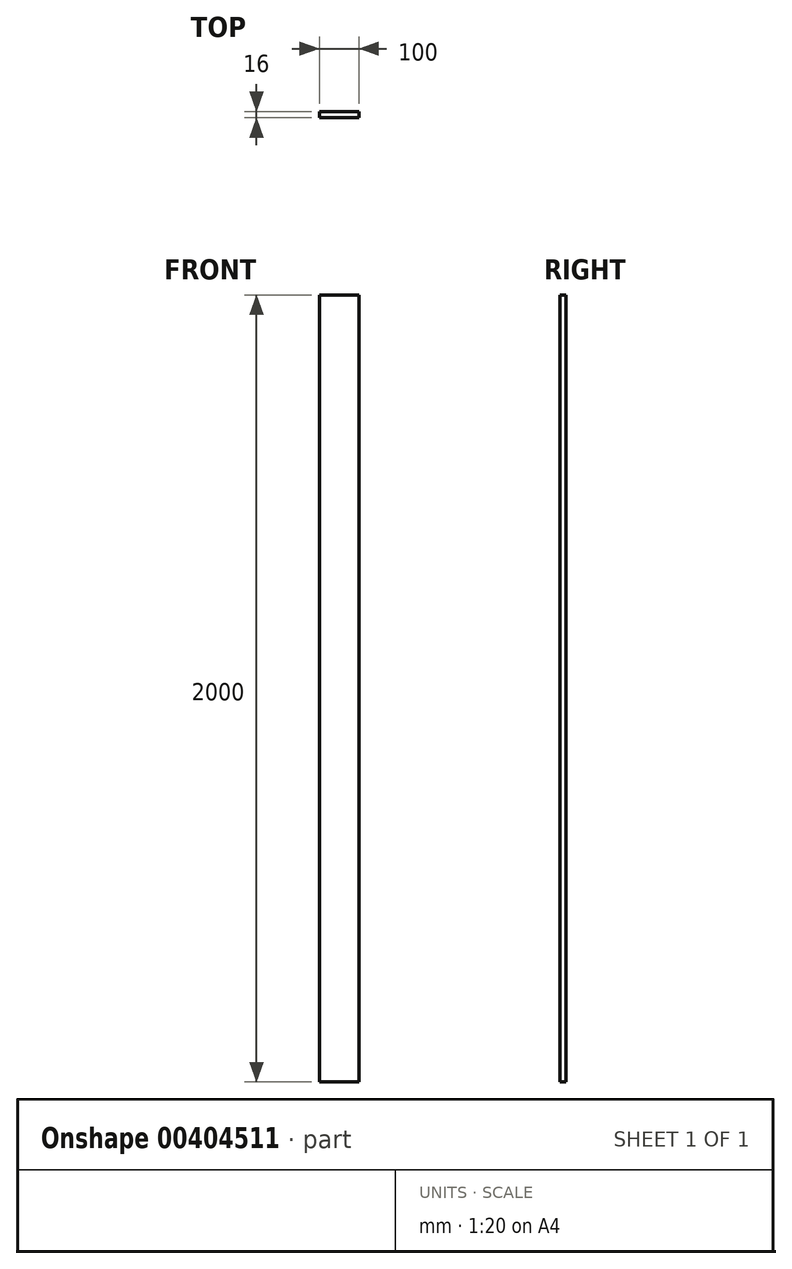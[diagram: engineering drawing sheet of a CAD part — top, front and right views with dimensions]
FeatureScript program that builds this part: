
annotation { "Feature Type Name" : "Feature", "Feature Type Description" : "" }
export const myFeature = defineFeature(function(context is Context, id is Id, definition is map)
    precondition{}
    {
        {
            var Q0;
            Q0=qCreatedBy(makeId("Top.planeOp"),FACE);
            var sketch = newSketch(context, id + "F0", { "sketchPlane" : qUnion([Q0])});
            skLineSegment(sketch, "E0.bottom", {"start": v(0, 0) * mm, "end": v(61.34, 0) * mm});
            skLineSegment(sketch, "E0.top", {"start": v(0, -59.54) * mm, "end": v(61.34, -59.54) * mm});
            skLineSegment(sketch, "E0.left", {"start": v(0, 0) * mm, "end": v(0, -59.54) * mm});
            skLineSegment(sketch, "E0.right", {"start": v(61.34, 0) * mm, "end": v(61.34, -59.54) * mm});
            skSolve(sketch);
        }
        {
            var Q0;
            Q0=makeQuery(id+"F0.imprint","IMPRINT",FACE,{"disambiguationData":[TD([[makeQuery(id+"F0.imprint","IMPRINT",EDGE,{"derivedFrom":sQuery(id+"F0.wireOp",EDGE,"E0.bottom")}),-1.0]])]});
            extrude(context, id + "F1", {"entities" : qUnion([Q0]), "depth" : 16 * mm});
        }
        {
            var Q0;
            Q0=makeQuery(id+"F1.opExtrude","SWEPT_FACE",FACE,{"disambiguationData":[OSD([sQuery(id+"F0.wireOp",EDGE,"E0.bottom")])]});
            extrude(context, id + "F2", {"entities" : qUnion([Q0]), "operationType" : NewBodyOperationType.INTERSECT, "oppositeDirection" : true, "depth" : 16 * mm});
        }
        {
            var Q0;
            Q0=makeQuery(id+"F1.opExtrude","CAP_FACE",FACE,{"disambiguationData":[OSD([sQuery(id+"F0.wireOp",EDGE,"E0.bottom"),sQuery(id+"F0.wireOp",EDGE,"E0.top"),sQuery(id+"F0.wireOp",EDGE,"E0.left"),sQuery(id+"F0.wireOp",EDGE,"E0.right")])],"isStart":true});
            extrude(context, id + "F3", {"entities" : qUnion([Q0]), "operationType" : NewBodyOperationType.ADD, "oppositeDirection" : true, "depth" : 2000 * mm});
        }
        {
            var Q0;
            {var subQ0=sQuery(id+"F0.wireOp",EDGE,"E0.left");Q0=makeQuery(id+"F3.boolean.opBoolean","MERGE",FACE,{"derivedFrom":[makeQuery(id+"F1.opExtrude","SWEPT_FACE",FACE,{"disambiguationData":[OSD([subQ0])]}),makeQuery(id+"F3.opExtrude","SWEPT_FACE",FACE,{"disambiguationData":[OSD([subQ0])]})]});}
            extrude(context, id + "F4", {"entities" : qUnion([Q0]), "operationType" : NewBodyOperationType.ADD, "oppositeDirection" : true, "depth" : 100 * mm});
        }
    });
